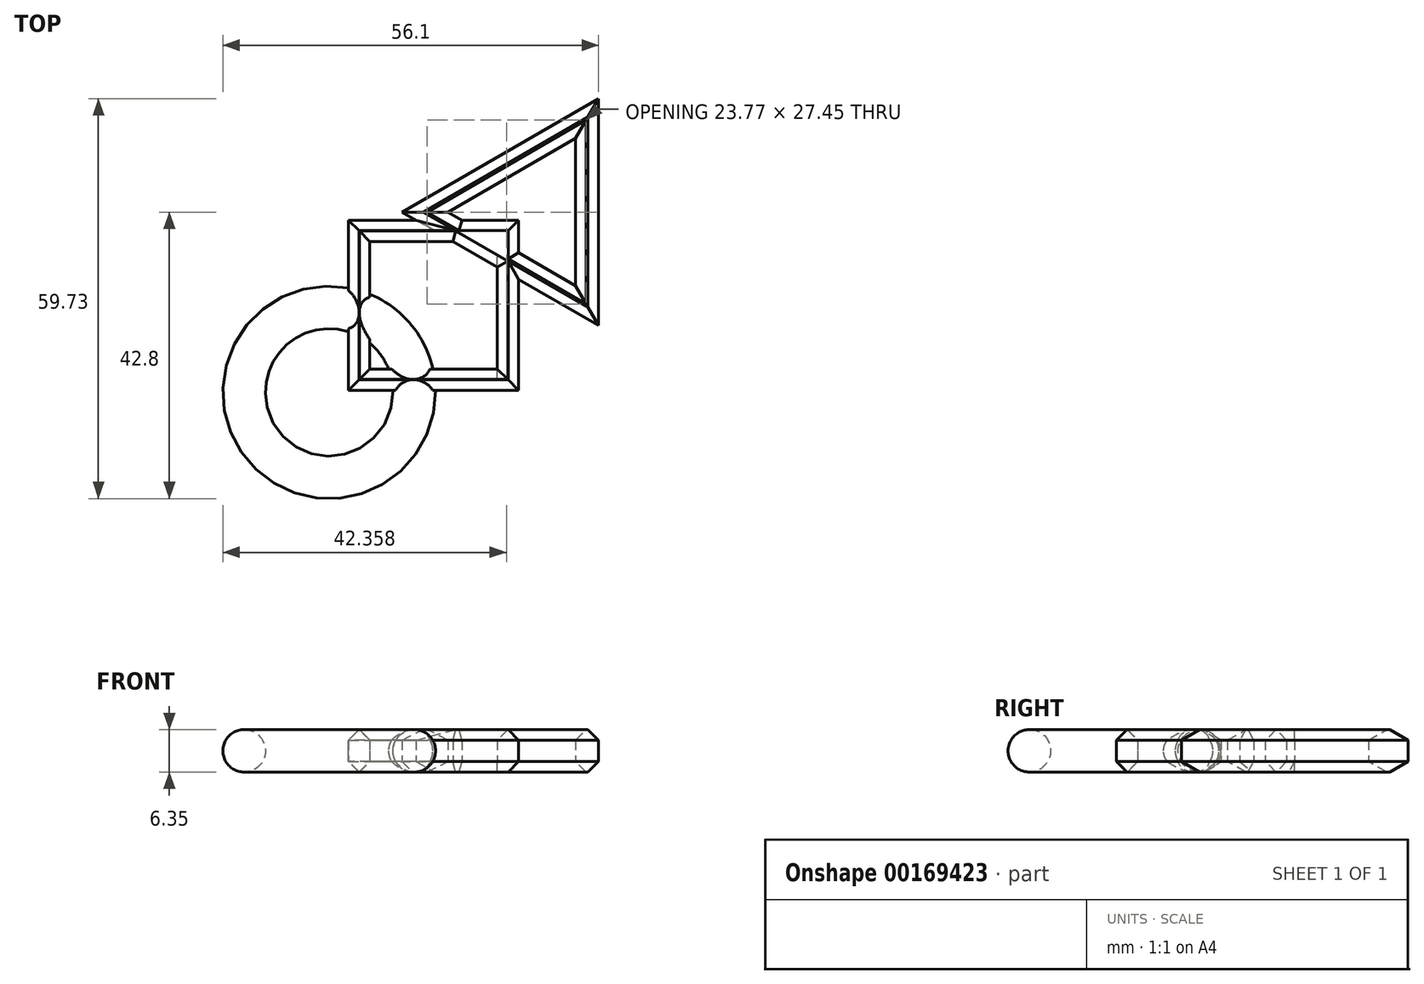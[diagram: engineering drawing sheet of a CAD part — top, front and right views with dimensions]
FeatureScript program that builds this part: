
annotation { "Feature Type Name" : "Feature", "Feature Type Description" : "" }
export const myFeature = defineFeature(function(context is Context, id is Id, definition is map)
    precondition{}
    {
        {
            var Q0;
            Q0=qCreatedBy(makeId("Top.planeOp"),FACE);
            var sketch = newSketch(context, id + "F0", { "sketchPlane" : qUnion([Q0])});
            skCircle(sketch, "E0.cCircle", {"center": v(0, 0) * mm, "radius": 6.35 * mm, "construction": true});
            skLineSegment(sketch, "E0.0", {"start": v(6.35, 11) * mm, "end": v(6.35, -11) * mm});
            skLineSegment(sketch, "E0.1", {"start": v(6.35, -11) * mm, "end": v(-12.7, 0) * mm});
            skLineSegment(sketch, "E0.2", {"start": v(-12.7, 0) * mm, "end": v(6.35, 11) * mm});
            skPoint(sketch, "E0.0.midPoint", {"position": v(6.35, 0) * mm});
            skCircle(sketch, "E1.cCircle", {"center": v(0, 0) * mm, "radius": 9.78 * mm, "construction": true});
            skLineSegment(sketch, "E1.0", {"start": v(-19.55, 0) * mm, "end": v(9.78, 16.93) * mm});
            skLineSegment(sketch, "E1.1", {"start": v(9.78, 16.93) * mm, "end": v(9.78, -16.93) * mm});
            skLineSegment(sketch, "E1.2", {"start": v(9.78, -16.93) * mm, "end": v(-19.55, 0) * mm});
            skPoint(sketch, "E1.0.midPoint", {"position": v(-4.89, 8.47) * mm});
            skLineSegment(sketch, "E2.bottom", {"start": v(-2.15, -1.2) * mm, "end": v(-27.55, -1.2) * mm});
            skLineSegment(sketch, "E2.top", {"start": v(-2.15, -26.6) * mm, "end": v(-27.55, -26.6) * mm});
            skLineSegment(sketch, "E2.left", {"start": v(-2.15, -1.2) * mm, "end": v(-2.15, -26.6) * mm});
            skLineSegment(sketch, "E2.right", {"start": v(-27.55, -1.2) * mm, "end": v(-27.55, -26.6) * mm});
            skLineSegment(sketch, "E3.bottom", {"start": v(-24.37, -4.38) * mm, "end": v(-5.32, -4.38) * mm});
            skLineSegment(sketch, "E3.top", {"start": v(-24.37, -23.43) * mm, "end": v(-5.32, -23.43) * mm});
            skLineSegment(sketch, "E3.left", {"start": v(-24.37, -4.38) * mm, "end": v(-24.37, -23.43) * mm});
            skLineSegment(sketch, "E3.right", {"start": v(-5.32, -4.38) * mm, "end": v(-5.32, -23.43) * mm});
            skPoint(sketch, "E3.middle", {"position": v(-14.85, -13.9) * mm});
            skCircle(sketch, "E4", {"center": v(-30.45, -26.93) * mm, "radius": 15.88 * mm});
            skPoint(sketch, "E4.first.point", {"position": v(-17.46, -17.8) * mm});
            skPoint(sketch, "E4.second.point", {"position": v(-42.43, -37.33) * mm});
            skPoint(sketch, "E4.third.point", {"position": v(-44.92, -33.46) * mm});
            skCircle(sketch, "E5.0", {"center": v(-30.45, -26.93) * mm, "radius": 9.52 * mm});
            skSolve(sketch);
        }
        {
            var Q0;
            {var subQ0=sQuery(id+"F0.wireOp",EDGE,"E4");var subQ1=sQuery(id+"F0.wireOp",EDGE,"E2.top");var subQ2=makeQuery(id+"F0.imprint","INTERSECT",VERTEX,{"derivedFrom":[subQ1,subQ0]});Q0=makeQuery(id+"F0.imprint","IMPRINT",FACE,{"disambiguationData":[TD([[makeQuery(id+"F0.imprint","IMPRINT",EDGE,{"disambiguationData":[TD([[subQ2,-1.0]])],"derivedFrom":subQ1}),1.0]])]});}
            var Q1;
            {var subQ3=sQuery(id+"F0.wireOp",EDGE,"E4");var subQ10=sQuery(id+"F0.wireOp",EDGE,"E2.top");var subQ11=makeQuery(id+"F0.imprint","INTERSECT",VERTEX,{"derivedFrom":[subQ10,subQ3]});Q1=makeQuery(id+"F0.imprint","IMPRINT",FACE,{"disambiguationData":[TD([[makeQuery(id+"F0.imprint","IMPRINT",EDGE,{"disambiguationData":[TD([[subQ11,-1.0]])],"derivedFrom":subQ10}),-1.0]])]});}
            var Q2;
            {var subQ0=sQuery(id+"F0.wireOp",EDGE,"E2.right");var subQ1=sQuery(id+"F0.wireOp",EDGE,"E2.top");var subQ2=makeQuery(id+"F0.imprint","INTERSECT",VERTEX,{"derivedFrom":[subQ1,subQ0]});Q2=makeQuery(id+"F0.imprint","IMPRINT",FACE,{"disambiguationData":[TD([[makeQuery(id+"F0.imprint","IMPRINT",EDGE,{"disambiguationData":[TD([[subQ2,1.0]])],"derivedFrom":subQ1}),-1.0]])]});}
            var Q3;
            {var subQ0=sQuery(id+"F0.wireOp",EDGE,"E2.left");var subQ3=sQuery(id+"F0.wireOp",EDGE,"E1.2");var subQ4=makeQuery(id+"F0.imprint","INTERSECT",VERTEX,{"derivedFrom":[subQ3,subQ0]});Q3=makeQuery(id+"F0.imprint","IMPRINT",FACE,{"disambiguationData":[TD([[makeQuery(id+"F0.imprint","IMPRINT",EDGE,{"disambiguationData":[TD([[subQ4,-1.0]])],"derivedFrom":subQ3}),1.0]])]});}
            var Q4;
            {var subQ1=sQuery(id+"F0.wireOp",EDGE,"E2.bottom");var subQ9=sQuery(id+"F0.wireOp",EDGE,"E1.2");var subQ10=makeQuery(id+"F0.imprint","INTERSECT",VERTEX,{"derivedFrom":[subQ9,subQ1]});Q4=makeQuery(id+"F0.imprint","IMPRINT",FACE,{"disambiguationData":[TD([[makeQuery(id+"F0.imprint","IMPRINT",EDGE,{"disambiguationData":[TD([[subQ10,1.0]])],"derivedFrom":subQ9}),1.0]])]});}
            var Q5;
            {var subQ3=sQuery(id+"F0.wireOp",EDGE,"E0.1");var subQ10=sQuery(id+"F0.wireOp",EDGE,"E2.left");var subQ12=makeQuery(id+"F0.imprint","INTERSECT",VERTEX,{"derivedFrom":[subQ3,subQ10]});Q5=makeQuery(id+"F0.imprint","IMPRINT",FACE,{"disambiguationData":[TD([[makeQuery(id+"F0.imprint","IMPRINT",EDGE,{"disambiguationData":[TD([[subQ12,-1.0]])],"derivedFrom":subQ3}),1.0]])]});}
            var Q6;
            {var subQ0=sQuery(id+"F0.wireOp",EDGE,"E2.left");var subQ1=sQuery(id+"F0.wireOp",EDGE,"E0.1");var subQ2=makeQuery(id+"F0.imprint","INTERSECT",VERTEX,{"derivedFrom":[subQ1,subQ0]});Q6=makeQuery(id+"F0.imprint","IMPRINT",FACE,{"disambiguationData":[TD([[makeQuery(id+"F0.imprint","IMPRINT",EDGE,{"disambiguationData":[TD([[subQ2,-1.0]])],"derivedFrom":subQ1}),-1.0]])]});}
            var Q7;
            {var subQ4=sQuery(id+"F0.wireOp",EDGE,"E0.0");Q7=makeQuery(id+"F0.imprint","IMPRINT",FACE,{"disambiguationData":[TD([[makeQuery(id+"F0.imprint","IMPRINT",EDGE,{"derivedFrom":subQ4}),1.0]])]});}
            var Q8;
            {var subQ0=sQuery(id+"F0.wireOp",EDGE,"E4");var subQ1=sQuery(id+"F0.wireOp",EDGE,"E2.right");var subQ2=makeQuery(id+"F0.imprint","INTERSECT",VERTEX,{"derivedFrom":[subQ1,subQ0]});Q8=makeQuery(id+"F0.imprint","IMPRINT",FACE,{"disambiguationData":[TD([[makeQuery(id+"F0.imprint","IMPRINT",EDGE,{"disambiguationData":[TD([[subQ2,-1.0]])],"derivedFrom":subQ1}),1.0]])]});}
            var Q9;
            {var subQ0=sQuery(id+"F0.wireOp",EDGE,"E5.0");var subQ1=sQuery(id+"F0.wireOp",EDGE,"E3.top");var subQ2=makeQuery(id+"F0.imprint","INTERSECT",VERTEX,{"derivedFrom":[subQ1,subQ0]});Q9=makeQuery(id+"F0.imprint","IMPRINT",FACE,{"disambiguationData":[TD([[makeQuery(id+"F0.imprint","IMPRINT",EDGE,{"disambiguationData":[TD([[subQ2,-1.0]])],"derivedFrom":subQ1}),1.0]])]});}
            var Q10;
            {var subQ0=sQuery(id+"F0.wireOp",EDGE,"E3.right");var subQ1=sQuery(id+"F0.wireOp",EDGE,"E1.2");var subQ2=makeQuery(id+"F0.imprint","INTERSECT",VERTEX,{"derivedFrom":[subQ1,subQ0]});Q10=makeQuery(id+"F0.imprint","IMPRINT",FACE,{"disambiguationData":[TD([[makeQuery(id+"F0.imprint","IMPRINT",EDGE,{"disambiguationData":[TD([[subQ2,-1.0]])],"derivedFrom":subQ1}),-1.0]])]});}
            extrude(context, id + "F1", {"entities" : qUnion([Q0, Q1, Q2, Q3, Q4, Q5, Q6, Q7, Q8, Q9, Q10]), "depth" : 6.35 * mm});
        }
        {
            var Q0;
            {var subQ0=sQuery(id+"F0.wireOp",EDGE,"E4");Q0=makeQuery(id+"F1.opExtrude","CAP_EDGE",EDGE,{"disambiguationData":[OSD([subQ0]),TDD([makeQuery(id+"F0.imprint","IMPRINT",EDGE,{"disambiguationData":[TD([[makeQuery(id+"F0.imprint","INTERSECT",VERTEX,{"derivedFrom":[sQuery(id+"F0.wireOp",EDGE,"E2.top"),subQ0]}),1.0]])],"derivedFrom":subQ0})])],"isStart":false});}
            var Q1;
            {var subQ0=sQuery(id+"F0.wireOp",EDGE,"E5.0");Q1=makeQuery(id+"F1.opExtrude","CAP_EDGE",EDGE,{"disambiguationData":[OSD([subQ0]),TDD([makeQuery(id+"F0.imprint","IMPRINT",EDGE,{"disambiguationData":[TD([[makeQuery(id+"F0.imprint","INTERSECT",VERTEX,{"derivedFrom":[sQuery(id+"F0.wireOp",EDGE,"E2.top"),subQ0]}),1.0]])],"derivedFrom":subQ0})])],"isStart":false});}
            var Q2;
            {var subQ0=sQuery(id+"F0.wireOp",EDGE,"E5.0");Q2=makeQuery(id+"F1.opExtrude","CAP_EDGE",EDGE,{"disambiguationData":[OSD([subQ0]),TDD([makeQuery(id+"F0.imprint","IMPRINT",EDGE,{"disambiguationData":[TD([[makeQuery(id+"F0.imprint","INTERSECT",VERTEX,{"derivedFrom":[sQuery(id+"F0.wireOp",EDGE,"E3.top"),subQ0]}),-1.0]])],"derivedFrom":subQ0})])],"isStart":false});}
            var Q3;
            {var subQ0=sQuery(id+"F0.wireOp",EDGE,"E4");Q3=makeQuery(id+"F1.opExtrude","CAP_EDGE",EDGE,{"disambiguationData":[OSD([subQ0]),TDD([makeQuery(id+"F0.imprint","IMPRINT",EDGE,{"disambiguationData":[TD([[makeQuery(id+"F0.imprint","INTERSECT",VERTEX,{"derivedFrom":[sQuery(id+"F0.wireOp",EDGE,"E3.top"),subQ0]}),-1.0]])],"derivedFrom":subQ0})])],"isStart":false});}
            fillet(context, id + "F2", {"entities" : qUnion([Q0, Q1, Q2, Q3]), "radius" : 3.17 * mm, "tangentPropagation" : true, "allowEdgeOverflow" : false});
        }
        {
            var Q0;
            {var subQ0=sQuery(id+"F0.wireOp",EDGE,"E2.top");Q0=makeQuery(id+"F1.opExtrude","CAP_EDGE",EDGE,{"disambiguationData":[OSD([subQ0]),TDD([makeQuery(id+"F0.imprint","IMPRINT",EDGE,{"disambiguationData":[TD([[makeQuery(id+"F0.imprint","INTERSECT",VERTEX,{"derivedFrom":[subQ0,sQuery(id+"F0.wireOp",EDGE,"E2.left")]}),-1.0]])],"derivedFrom":subQ0})])],"isStart":false});}
            var Q1;
            {var subQ0=sQuery(id+"F0.wireOp",EDGE,"E3.top");Q1=makeQuery(id+"F1.opExtrude","CAP_EDGE",EDGE,{"disambiguationData":[OSD([subQ0]),TDD([makeQuery(id+"F0.imprint","IMPRINT",EDGE,{"disambiguationData":[TD([[makeQuery(id+"F0.imprint","INTERSECT",VERTEX,{"derivedFrom":[subQ0,sQuery(id+"F0.wireOp",EDGE,"E3.right")]}),1.0]])],"derivedFrom":subQ0})])],"isStart":false});}
            var Q2;
            {var subQ0=sQuery(id+"F0.wireOp",EDGE,"E2.left");Q2=makeQuery(id+"F1.opExtrude","CAP_EDGE",EDGE,{"disambiguationData":[OSD([subQ0]),TDD([makeQuery(id+"F0.imprint","IMPRINT",EDGE,{"disambiguationData":[TD([[makeQuery(id+"F0.imprint","INTERSECT",VERTEX,{"derivedFrom":[sQuery(id+"F0.wireOp",EDGE,"E2.top"),subQ0]}),1.0]])],"derivedFrom":subQ0})])],"isStart":false});}
            var Q3;
            Q3=makeQuery(id+"F1.opExtrude","CAP_EDGE",EDGE,{"disambiguationData":[OSD([sQuery(id+"F0.wireOp",EDGE,"E3.right")])],"isStart":false});
            var Q4;
            {var subQ0=sQuery(id+"F0.wireOp",EDGE,"E3.left");Q4=makeQuery(id+"F1.opExtrude","CAP_EDGE",EDGE,{"disambiguationData":[OSD([subQ0]),TDD([makeQuery(id+"F0.imprint","IMPRINT",EDGE,{"disambiguationData":[TD([[makeQuery(id+"F0.imprint","INTERSECT",VERTEX,{"derivedFrom":[sQuery(id+"F0.wireOp",EDGE,"E3.top"),subQ0]}),1.0]])],"derivedFrom":subQ0})])],"isStart":false});}
            var Q5;
            {var subQ0=sQuery(id+"F0.wireOp",EDGE,"E2.right");Q5=makeQuery(id+"F1.opExtrude","CAP_EDGE",EDGE,{"disambiguationData":[OSD([subQ0]),TDD([makeQuery(id+"F0.imprint","IMPRINT",EDGE,{"disambiguationData":[TD([[makeQuery(id+"F0.imprint","INTERSECT",VERTEX,{"derivedFrom":[sQuery(id+"F0.wireOp",EDGE,"E2.top"),subQ0]}),1.0]])],"derivedFrom":subQ0})])],"isStart":false});}
            var Q6;
            Q6=makeQuery(id+"F1.opExtrude","CAP_EDGE",EDGE,{"disambiguationData":[OSD([sQuery(id+"F0.wireOp",EDGE,"E3.bottom")])],"isStart":false});
            var Q7;
            {var subQ0=sQuery(id+"F0.wireOp",EDGE,"E2.bottom");Q7=makeQuery(id+"F1.opExtrude","CAP_EDGE",EDGE,{"disambiguationData":[OSD([subQ0]),TDD([makeQuery(id+"F0.imprint","IMPRINT",EDGE,{"disambiguationData":[TD([[makeQuery(id+"F0.imprint","INTERSECT",VERTEX,{"derivedFrom":[subQ0,sQuery(id+"F0.wireOp",EDGE,"E2.right")]}),1.0]])],"derivedFrom":subQ0})])],"isStart":false});}
            var Q8;
            {var subQ0=sQuery(id+"F0.wireOp",EDGE,"E2.bottom");Q8=makeQuery(id+"F1.opExtrude","CAP_EDGE",EDGE,{"disambiguationData":[OSD([subQ0]),TDD([makeQuery(id+"F0.imprint","IMPRINT",EDGE,{"disambiguationData":[TD([[makeQuery(id+"F0.imprint","INTERSECT",VERTEX,{"derivedFrom":[subQ0,sQuery(id+"F0.wireOp",EDGE,"E2.left")]}),-1.0]])],"derivedFrom":subQ0})])],"isStart":false});}
            var Q9;
            Q9=makeQuery(id+"F1.opExtrude","CAP_FACE",FACE,{"disambiguationData":[OSD([sQuery(id+"F0.wireOp",EDGE,"E0.0"),sQuery(id+"F0.wireOp",EDGE,"E0.1"),sQuery(id+"F0.wireOp",EDGE,"E0.2"),sQuery(id+"F0.wireOp",EDGE,"E1.0"),sQuery(id+"F0.wireOp",EDGE,"E1.1"),sQuery(id+"F0.wireOp",EDGE,"E1.2"),sQuery(id+"F0.wireOp",EDGE,"E2.bottom"),sQuery(id+"F0.wireOp",EDGE,"E2.top"),sQuery(id+"F0.wireOp",EDGE,"E2.left"),sQuery(id+"F0.wireOp",EDGE,"E2.right"),sQuery(id+"F0.wireOp",EDGE,"E3.bottom"),sQuery(id+"F0.wireOp",EDGE,"E3.top"),sQuery(id+"F0.wireOp",EDGE,"E3.left"),sQuery(id+"F0.wireOp",EDGE,"E3.right"),sQuery(id+"F0.wireOp",EDGE,"E4"),sQuery(id+"F0.wireOp",EDGE,"E5.0")])],"isStart":false});
            chamfer(context, id + "F3", {"entities" : qUnion([Q0, Q1, Q2, Q3, Q4, Q5, Q6, Q7, Q8, Q9]), "width" : 1.57 * mm, "tangentPropagation" : true});
        }
        {
            var Q0;
            {var subQ0=sQuery(id+"F0.wireOp",EDGE,"E4");Q0=makeQuery(id+"F1.opExtrude","CAP_EDGE",EDGE,{"disambiguationData":[OSD([subQ0]),TDD([makeQuery(id+"F0.imprint","IMPRINT",EDGE,{"disambiguationData":[TD([[makeQuery(id+"F0.imprint","INTERSECT",VERTEX,{"derivedFrom":[sQuery(id+"F0.wireOp",EDGE,"E2.top"),subQ0]}),1.0]])],"derivedFrom":subQ0})])],"isStart":true});}
            var Q1;
            {var subQ0=sQuery(id+"F0.wireOp",EDGE,"E5.0");Q1=makeQuery(id+"F1.opExtrude","CAP_EDGE",EDGE,{"disambiguationData":[OSD([subQ0]),TDD([makeQuery(id+"F0.imprint","IMPRINT",EDGE,{"disambiguationData":[TD([[makeQuery(id+"F0.imprint","INTERSECT",VERTEX,{"derivedFrom":[sQuery(id+"F0.wireOp",EDGE,"E2.top"),subQ0]}),1.0]])],"derivedFrom":subQ0})])],"isStart":true});}
            var Q2;
            {var subQ0=sQuery(id+"F0.wireOp",EDGE,"E4");Q2=makeQuery(id+"F1.opExtrude","CAP_EDGE",EDGE,{"disambiguationData":[OSD([subQ0]),TDD([makeQuery(id+"F0.imprint","IMPRINT",EDGE,{"disambiguationData":[TD([[makeQuery(id+"F0.imprint","INTERSECT",VERTEX,{"derivedFrom":[sQuery(id+"F0.wireOp",EDGE,"E3.top"),subQ0]}),-1.0]])],"derivedFrom":subQ0})])],"isStart":true});}
            var Q3;
            {var subQ0=sQuery(id+"F0.wireOp",EDGE,"E5.0");Q3=makeQuery(id+"F1.opExtrude","CAP_EDGE",EDGE,{"disambiguationData":[OSD([subQ0]),TDD([makeQuery(id+"F0.imprint","IMPRINT",EDGE,{"disambiguationData":[TD([[makeQuery(id+"F0.imprint","INTERSECT",VERTEX,{"derivedFrom":[sQuery(id+"F0.wireOp",EDGE,"E3.top"),subQ0]}),-1.0]])],"derivedFrom":subQ0})])],"isStart":true});}
            fillet(context, id + "F4", {"entities" : qUnion([Q0, Q1, Q2, Q3]), "radius" : 3.17 * mm, "tangentPropagation" : true, "allowEdgeOverflow" : false});
        }
        {
            var Q0;
            {var subQ0=sQuery(id+"F0.wireOp",EDGE,"E2.top");Q0=makeQuery(id+"F1.opExtrude","CAP_EDGE",EDGE,{"disambiguationData":[OSD([subQ0]),TDD([makeQuery(id+"F0.imprint","IMPRINT",EDGE,{"disambiguationData":[TD([[makeQuery(id+"F0.imprint","INTERSECT",VERTEX,{"derivedFrom":[subQ0,sQuery(id+"F0.wireOp",EDGE,"E2.right")]}),1.0]])],"derivedFrom":subQ0})])],"isStart":true});}
            var Q1;
            {var subQ0=sQuery(id+"F0.wireOp",EDGE,"E2.left");Q1=makeQuery(id+"F1.opExtrude","CAP_EDGE",EDGE,{"disambiguationData":[OSD([subQ0]),TDD([makeQuery(id+"F0.imprint","IMPRINT",EDGE,{"disambiguationData":[TD([[makeQuery(id+"F0.imprint","INTERSECT",VERTEX,{"derivedFrom":[sQuery(id+"F0.wireOp",EDGE,"E2.top"),subQ0]}),1.0]])],"derivedFrom":subQ0})])],"isStart":true});}
            var Q2;
            {var subQ0=sQuery(id+"F0.wireOp",EDGE,"E3.top");Q2=makeQuery(id+"F1.opExtrude","CAP_EDGE",EDGE,{"disambiguationData":[OSD([subQ0]),TDD([makeQuery(id+"F0.imprint","IMPRINT",EDGE,{"disambiguationData":[TD([[makeQuery(id+"F0.imprint","INTERSECT",VERTEX,{"derivedFrom":[subQ0,sQuery(id+"F0.wireOp",EDGE,"E3.right")]}),1.0]])],"derivedFrom":subQ0})])],"isStart":true});}
            var Q3;
            {var subQ0=sQuery(id+"F0.wireOp",EDGE,"E3.left");Q3=makeQuery(id+"F1.opExtrude","CAP_EDGE",EDGE,{"disambiguationData":[OSD([subQ0]),TDD([makeQuery(id+"F0.imprint","IMPRINT",EDGE,{"disambiguationData":[TD([[makeQuery(id+"F0.imprint","INTERSECT",VERTEX,{"derivedFrom":[sQuery(id+"F0.wireOp",EDGE,"E3.top"),subQ0]}),1.0]])],"derivedFrom":subQ0})])],"isStart":true});}
            var Q4;
            {var subQ0=sQuery(id+"F0.wireOp",EDGE,"E2.right");Q4=makeQuery(id+"F1.opExtrude","CAP_EDGE",EDGE,{"disambiguationData":[OSD([subQ0]),TDD([makeQuery(id+"F0.imprint","IMPRINT",EDGE,{"disambiguationData":[TD([[makeQuery(id+"F0.imprint","INTERSECT",VERTEX,{"derivedFrom":[sQuery(id+"F0.wireOp",EDGE,"E2.top"),subQ0]}),1.0]])],"derivedFrom":subQ0})])],"isStart":true});}
            var Q5;
            Q5=makeQuery(id+"F1.opExtrude","CAP_EDGE",EDGE,{"disambiguationData":[OSD([sQuery(id+"F0.wireOp",EDGE,"E3.bottom")])],"isStart":true});
            var Q6;
            {var subQ0=sQuery(id+"F0.wireOp",EDGE,"E1.2");Q6=makeQuery(id+"F1.opExtrude","CAP_EDGE",EDGE,{"disambiguationData":[OSD([subQ0]),TDD([makeQuery(id+"F0.imprint","IMPRINT",EDGE,{"disambiguationData":[TD([[makeQuery(id+"F0.imprint","INTERSECT",VERTEX,{"derivedFrom":[subQ0,sQuery(id+"F0.wireOp",EDGE,"E3.right")]}),-1.0]])],"derivedFrom":subQ0})])],"isStart":true});}
            var Q7;
            {var subQ0=sQuery(id+"F0.wireOp",EDGE,"E2.left");Q7=makeQuery(id+"F1.opExtrude","CAP_EDGE",EDGE,{"disambiguationData":[OSD([subQ0]),TDD([makeQuery(id+"F0.imprint","IMPRINT",EDGE,{"disambiguationData":[TD([[makeQuery(id+"F0.imprint","INTERSECT",VERTEX,{"derivedFrom":[sQuery(id+"F0.wireOp",EDGE,"E2.bottom"),subQ0]}),-1.0]])],"derivedFrom":subQ0})])],"isStart":true});}
            var Q8;
            {var subQ0=sQuery(id+"F0.wireOp",EDGE,"E2.bottom");Q8=makeQuery(id+"F1.opExtrude","CAP_EDGE",EDGE,{"disambiguationData":[OSD([subQ0]),TDD([makeQuery(id+"F0.imprint","IMPRINT",EDGE,{"disambiguationData":[TD([[makeQuery(id+"F0.imprint","INTERSECT",VERTEX,{"derivedFrom":[subQ0,sQuery(id+"F0.wireOp",EDGE,"E2.left")]}),-1.0]])],"derivedFrom":subQ0})])],"isStart":true});}
            var Q9;
            {var subQ0=sQuery(id+"F0.wireOp",EDGE,"E2.bottom");Q9=makeQuery(id+"F1.opExtrude","CAP_EDGE",EDGE,{"disambiguationData":[OSD([subQ0]),TDD([makeQuery(id+"F0.imprint","IMPRINT",EDGE,{"disambiguationData":[TD([[makeQuery(id+"F0.imprint","INTERSECT",VERTEX,{"derivedFrom":[subQ0,sQuery(id+"F0.wireOp",EDGE,"E2.right")]}),1.0]])],"derivedFrom":subQ0})])],"isStart":true});}
            var Q10;
            Q10=makeQuery(id+"F1.opExtrude","CAP_EDGE",EDGE,{"disambiguationData":[OSD([sQuery(id+"F0.wireOp",EDGE,"E1.0")])],"isStart":true});
            var Q11;
            Q11=makeQuery(id+"F1.opExtrude","CAP_EDGE",EDGE,{"disambiguationData":[OSD([sQuery(id+"F0.wireOp",EDGE,"E1.1")])],"isStart":true});
            var Q12;
            {var subQ0=sQuery(id+"F0.wireOp",EDGE,"E1.2");Q12=makeQuery(id+"F1.opExtrude","CAP_EDGE",EDGE,{"disambiguationData":[OSD([subQ0]),TDD([makeQuery(id+"F0.imprint","IMPRINT",EDGE,{"disambiguationData":[TD([[makeQuery(id+"F0.imprint","INTERSECT",VERTEX,{"derivedFrom":[sQuery(id+"F0.wireOp",EDGE,"E1.1"),subQ0]}),-1.0]])],"derivedFrom":subQ0})])],"isStart":true});}
            var Q13;
            {var subQ0=sQuery(id+"F0.wireOp",EDGE,"E0.1");Q13=makeQuery(id+"F1.opExtrude","CAP_EDGE",EDGE,{"disambiguationData":[OSD([subQ0]),TDD([makeQuery(id+"F0.imprint","IMPRINT",EDGE,{"disambiguationData":[TD([[makeQuery(id+"F0.imprint","INTERSECT",VERTEX,{"derivedFrom":[sQuery(id+"F0.wireOp",EDGE,"E0.0"),subQ0]}),-1.0]])],"derivedFrom":subQ0})])],"isStart":true});}
            var Q14;
            {var subQ0=sQuery(id+"F0.wireOp",EDGE,"E0.1");Q14=makeQuery(id+"F1.opExtrude","CAP_EDGE",EDGE,{"disambiguationData":[OSD([subQ0]),TDD([makeQuery(id+"F0.imprint","IMPRINT",EDGE,{"disambiguationData":[TD([[makeQuery(id+"F0.imprint","INTERSECT",VERTEX,{"derivedFrom":[subQ0,sQuery(id+"F0.wireOp",EDGE,"E0.2")]}),1.0]])],"derivedFrom":subQ0})])],"isStart":true});}
            var Q15;
            Q15=makeQuery(id+"F1.opExtrude","CAP_EDGE",EDGE,{"disambiguationData":[OSD([sQuery(id+"F0.wireOp",EDGE,"E0.2")])],"isStart":true});
            var Q16;
            Q16=makeQuery(id+"F1.opExtrude","CAP_EDGE",EDGE,{"disambiguationData":[OSD([sQuery(id+"F0.wireOp",EDGE,"E0.0")])],"isStart":true});
            chamfer(context, id + "F5", {"entities" : qUnion([Q0, Q1, Q2, Q3, Q4, Q5, Q6, Q7, Q8, Q9, Q10, Q11, Q12, Q13, Q14, Q15, Q16]), "width" : 1.57 * mm, "tangentPropagation" : true});
        }
    });
